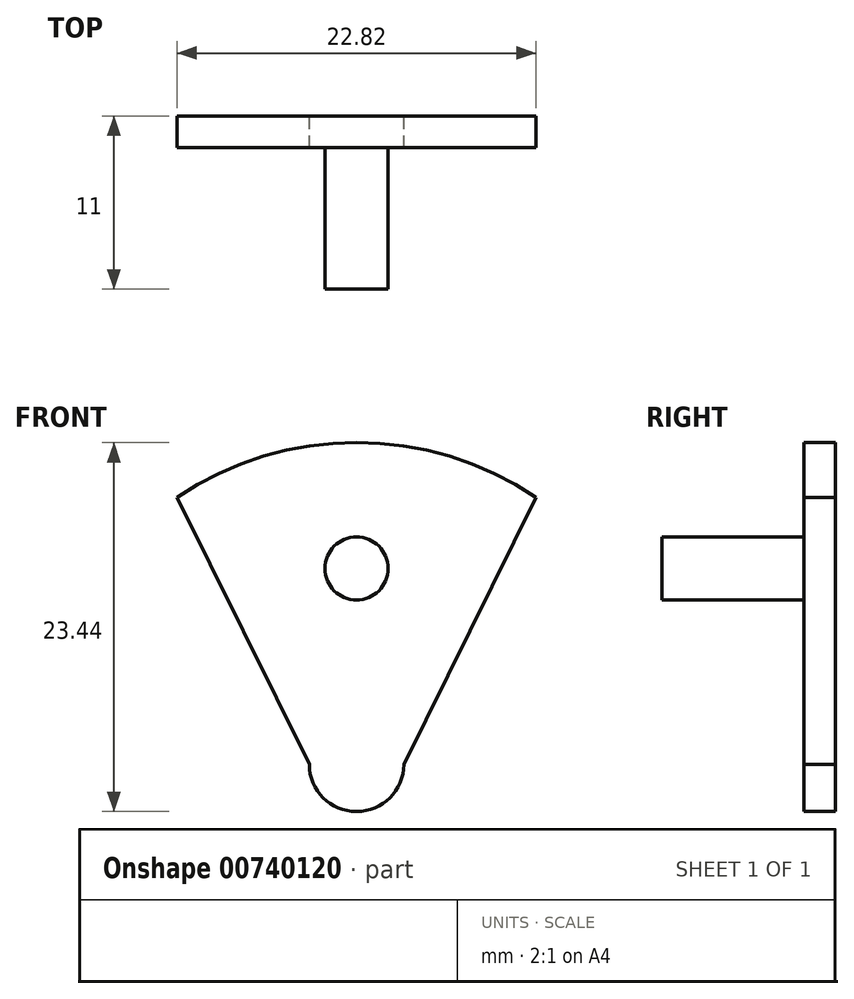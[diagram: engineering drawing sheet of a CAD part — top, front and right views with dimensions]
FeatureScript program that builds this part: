
annotation { "Feature Type Name" : "Feature", "Feature Type Description" : "" }
export const myFeature = defineFeature(function(context is Context, id is Id, definition is map)
    precondition{}
    {
        {
            var Q0;
            Q0=qCreatedBy(makeId("Front.planeOp"),FACE);
            var sketch = newSketch(context, id + "F0", { "sketchPlane" : qUnion([Q0])});
            skLineSegment(sketch, "E0", {"start": v(-3, 0) * mm, "end": v(-11.4, 16.97) * mm});
            skArc(sketch, "E1", {"start": v(-11.4, 16.97) * mm, "mid": v(-5.96, 19.56) * mm, "end": v(0, 20.44) * mm});
            skArc(sketch, "E2.MirrorCS", {"start": v(11.4, 16.97) * mm, "mid": v(5.96, 19.56) * mm, "end": v(0, 20.44) * mm});
            skLineSegment(sketch, "E3.MirrorCS", {"start": v(3, 0) * mm, "end": v(11.4, 16.97) * mm});
            skLineSegment(sketch, "E4", {"start": v(-3, 0) * mm, "end": v(3, 0) * mm});
            skSolve(sketch);
        }
        {
            var Q0;
            Q0 = qSketchRegion(id + "F0", true);
            extrude(context, id + "F1", {"entities" : qUnion([Q0]), "depth" : 2 * mm, "offsetDistance" : 25 * mm});
        }
        {
            var Q0;
            Q0=makeQuery(id+"F1.opExtrude","CAP_FACE",FACE,{"disambiguationData":[OSD([sQuery(id+"FT5xF7OF5X8uRs8_0.wireOp",EDGE,"o1QsFRFP-0LUh-9Q1L-VurE-56FqTLP4oNjF"),sQuery(id+"F0.wireOp",EDGE,"E0"),sQuery(id+"F0.wireOp",EDGE,"E1"),sQuery(id+"F0.wireOp",EDGE,"E2.MirrorCS"),sQuery(id+"F0.wireOp",EDGE,"E3.MirrorCS")])],"isStart":false});
            var sketch = newSketch(context, id + "F2", { "sketchPlane" : qUnion([Q0])});
            skCircle(sketch, "E5", {"center": v(0, 12.44) * mm, "radius": 2 * mm});
            skSolve(sketch);
        }
        {
            var Q0;
            Q0=makeQuery(id+"F2.imprint","IMPRINT",FACE,{"disambiguationData":[TD([[makeQuery(id+"F2.imprint","IMPRINT",EDGE,{"derivedFrom":sQuery(id+"F2.wireOp",EDGE,"E5")}),1.0]])]});
            extrude(context, id + "F3", {"entities" : qUnion([Q0]), "operationType" : NewBodyOperationType.ADD, "depth" : 9 * mm, "offsetDistance" : 25 * mm});
        }
        {
            var Q0;
            Q0=qCreatedBy(makeId("Front.planeOp"),FACE);
            var sketch = newSketch(context, id + "F4", { "sketchPlane" : qUnion([Q0])});
            skCircle(sketch, "E6", {"center": v(0, 0) * mm, "radius": 3 * mm});
            skSolve(sketch);
        }
        {
            var Q0;
            Q0=makeQuery(id+"F4.imprint","IMPRINT",FACE,{"disambiguationData":[TD([[makeQuery(id+"F4.imprint","IMPRINT",EDGE,{"derivedFrom":sQuery(id+"F4.wireOp",EDGE,"E6")}),1.0]])]});
            extrude(context, id + "F5", {"entities" : qUnion([Q0]), "operationType" : NewBodyOperationType.ADD, "depth" : 2 * mm, "offsetDistance" : 25 * mm});
        }
    });
